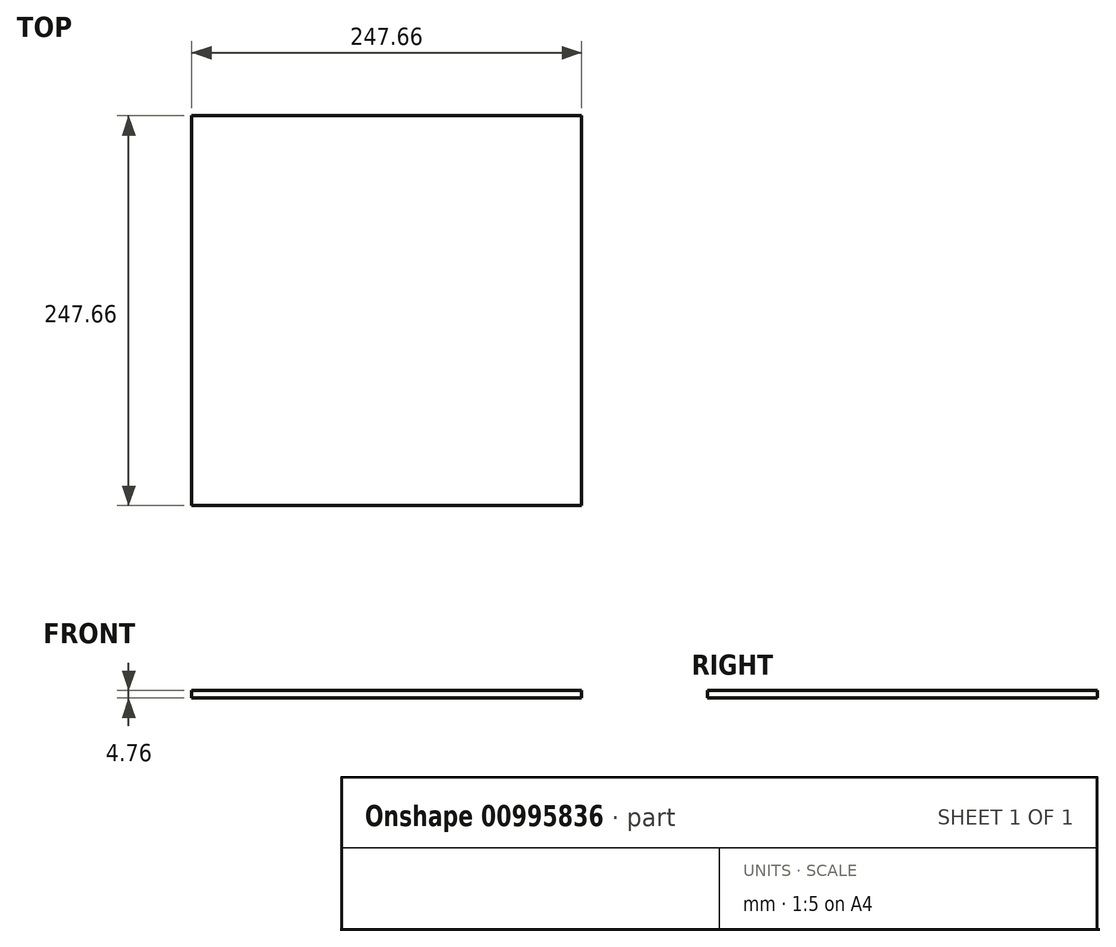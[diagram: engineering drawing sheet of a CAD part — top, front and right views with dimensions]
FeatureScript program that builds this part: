
annotation { "Feature Type Name" : "Feature", "Feature Type Description" : "" }
export const myFeature = defineFeature(function(context is Context, id is Id, definition is map)
    precondition{}
    {
        {
            var Q0;
            Q0=qCreatedBy(makeId("Top.planeOp"),FACE);
            var sketch = newSketch(context, id + "F0", { "sketchPlane" : qUnion([Q0])});
            skLineSegment(sketch, "E0.bottom", {"start": v(123.83, -123.83) * mm, "end": v(-123.83, -123.83) * mm});
            skLineSegment(sketch, "E0.top", {"start": v(123.83, 123.83) * mm, "end": v(-123.83, 123.83) * mm});
            skLineSegment(sketch, "E0.left", {"start": v(123.83, -123.83) * mm, "end": v(123.83, 123.83) * mm});
            skLineSegment(sketch, "E0.right", {"start": v(-123.83, -123.83) * mm, "end": v(-123.83, 123.83) * mm});
            skPoint(sketch, "E0.middle", {"position": v(0, 0) * mm});
            skSolve(sketch);
        }
        {
            var Q0;
            Q0=qSketchRegion(id+"F0",true);
            extrude(context, id + "F1", {"entities" : qUnion([Q0]), "depth" : 4.76 * mm, "offsetDistance" : 25.4 * mm});
        }
    });
